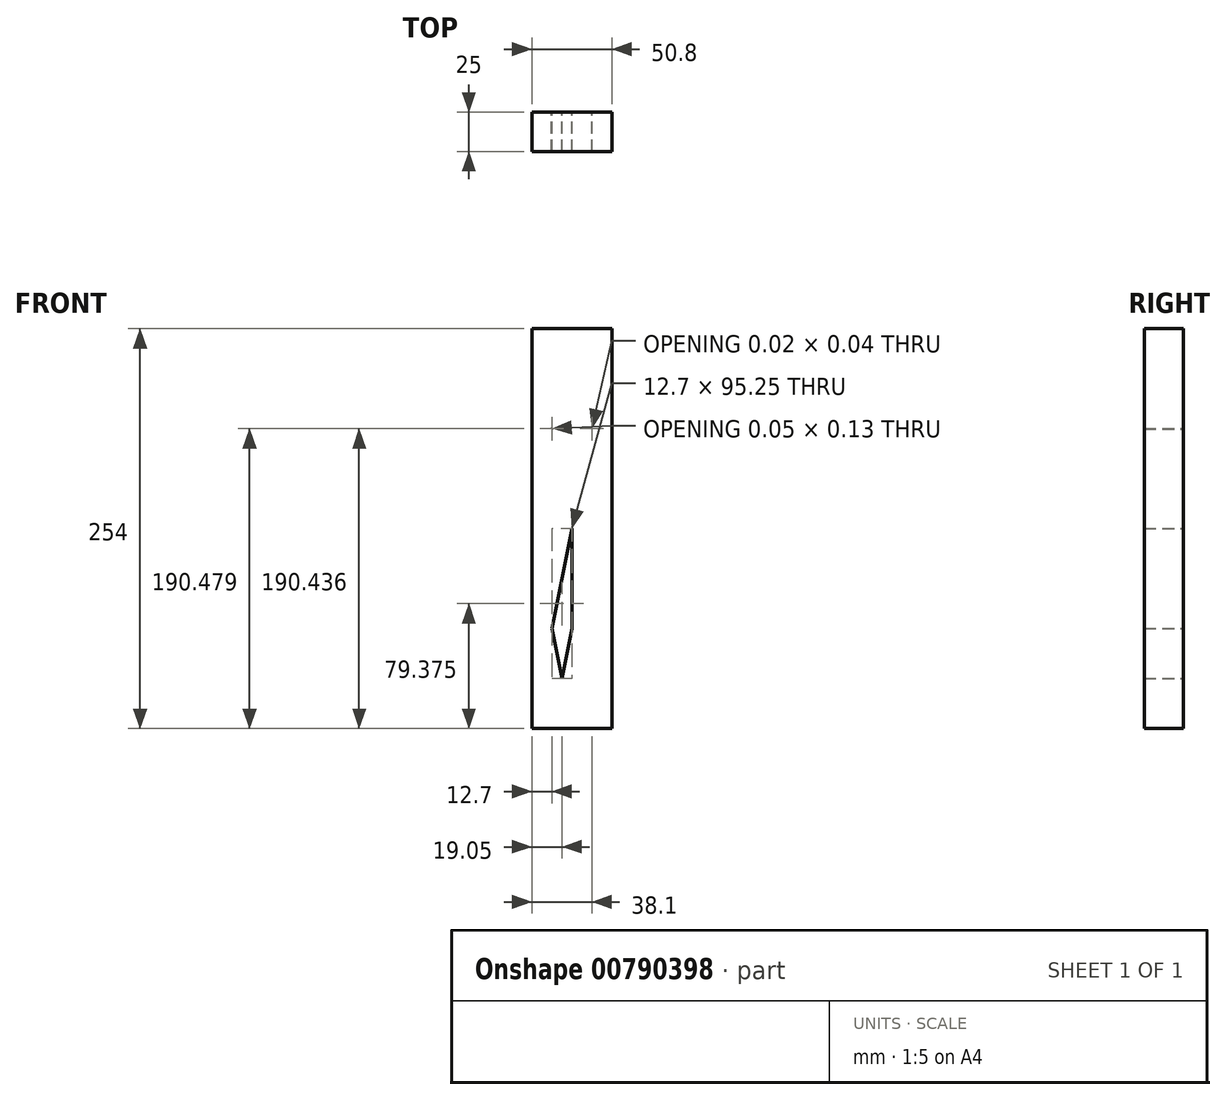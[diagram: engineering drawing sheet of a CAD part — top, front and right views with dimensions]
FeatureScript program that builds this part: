
annotation { "Feature Type Name" : "Feature", "Feature Type Description" : "" }
export const myFeature = defineFeature(function(context is Context, id is Id, definition is map)
    precondition{}
    {
        {
            var Q0;
            Q0=qCreatedBy(makeId("Front.planeOp"),FACE);
            var sketch = newSketch(context, id + "F0", { "sketchPlane" : qUnion([Q0])});
            skLineSegment(sketch, "E0.bottom", {"start": v(25.4, -127) * mm, "end": v(-25.4, -127) * mm});
            skLineSegment(sketch, "E0.top", {"start": v(25.4, 127) * mm, "end": v(-25.4, 127) * mm});
            skLineSegment(sketch, "E0.left", {"start": v(25.4, -127) * mm, "end": v(25.4, 127) * mm});
            skLineSegment(sketch, "E0.right", {"start": v(-25.4, -127) * mm, "end": v(-25.4, 127) * mm});
            skPoint(sketch, "E0.middle", {"position": v(0, 0) * mm});
            skLineSegment(sketch, "E1", {"start": v(-25.4, 127) * mm, "end": v(25.4, -127) * mm});
            skLineSegment(sketch, "E2", {"start": v(25.4, 127) * mm, "end": v(-25.4, -127) * mm});
            skLineSegment(sketch, "E3", {"start": v(0, 127) * mm, "end": v(0, -127) * mm});
            skLineSegment(sketch, "E4", {"start": v(0, -127) * mm, "end": v(-25.4, 0) * mm});
            skLineSegment(sketch, "E5", {"start": v(-25.4, 0) * mm, "end": v(25.4, 0) * mm});
            skLineSegment(sketch, "E6", {"start": v(25.4, 0) * mm, "end": v(0, -127) * mm});
            skLineSegment(sketch, "E7", {"start": v(-25.4, 0) * mm, "end": v(0, 127) * mm});
            skLineSegment(sketch, "E8", {"start": v(0, 127) * mm, "end": v(25.4, 0) * mm});
            skLineSegment(sketch, "E9", {"start": v(-12.7, 63.5) * mm, "end": v(-12.7, 0) * mm});
            skLineSegment(sketch, "E10", {"start": v(-12.7, 0) * mm, "end": v(-12.7, 127) * mm});
            skLineSegment(sketch, "E11", {"start": v(12.7, 0) * mm, "end": v(12.7, 127) * mm});
            skPoint(sketch, "E11.startSnap0", {"position": v(12.7, 63.5) * mm});
            skLineSegment(sketch, "E12", {"start": v(-12.7, 0) * mm, "end": v(-12.7, -127) * mm});
            skLineSegment(sketch, "E13", {"start": v(-12.7, -127) * mm, "end": v(12.7, 0) * mm});
            skLineSegment(sketch, "E14", {"start": v(12.7, 0) * mm, "end": v(12.7, -127) * mm});
            skLineSegment(sketch, "E15", {"start": v(-25.4, -63.5) * mm, "end": v(25.4, -63.5) * mm});
            skPoint(sketch, "E15.startSnap0", {"position": v(-12.7, -63.5) * mm});
            skPoint(sketch, "E15.endSnap0", {"position": v(12.7, -63.5) * mm});
            skLineSegment(sketch, "E16", {"start": v(-25.4, 63.33) * mm, "end": v(25.4, 63.5) * mm});
            skSolve(sketch);
        }
        {
            var Q0;
            {var subQ1=sQuery(id+"F0.wireOp",EDGE,"E0.left");var subQ3=sQuery(id+"F0.wireOp",EDGE,"E16");var subQ4=makeQuery(id+"F0.imprint","INTERSECT",VERTEX,{"derivedFrom":[subQ1,subQ3]});Q0=makeQuery(id+"F0.imprint","IMPRINT",FACE,{"disambiguationData":[TD([[makeQuery(id+"F0.imprint","IMPRINT",EDGE,{"disambiguationData":[TD([[subQ4,1.0]])],"derivedFrom":subQ3}),1.0]])]});}
            var Q1;
            {var subQ0=sQuery(id+"F0.wireOp",EDGE,"E13");var subQ1=sQuery(id+"F0.wireOp",EDGE,"E1");var subQ2=makeQuery(id+"F0.imprint","INTERSECT",VERTEX,{"derivedFrom":[subQ1,subQ0]});Q1=makeQuery(id+"F0.imprint","IMPRINT",FACE,{"disambiguationData":[TD([[makeQuery(id+"F0.imprint","IMPRINT",EDGE,{"disambiguationData":[TD([[subQ2,1.0]])],"derivedFrom":subQ1}),1.0]])]});}
            var Q2;
            {var subQ1=sQuery(id+"F0.wireOp",EDGE,"E0.bottom");var subQ3=sQuery(id+"F0.wireOp",EDGE,"E14");var subQ4=makeQuery(id+"F0.imprint","INTERSECT",VERTEX,{"derivedFrom":[subQ1,subQ3]});Q2=makeQuery(id+"F0.imprint","IMPRINT",FACE,{"disambiguationData":[TD([[makeQuery(id+"F0.imprint","IMPRINT",EDGE,{"disambiguationData":[TD([[subQ4,1.0]])],"derivedFrom":subQ1}),-1.0]])]});}
            var Q3;
            {var subQ1=sQuery(id+"F0.wireOp",EDGE,"E0.top");var subQ3=sQuery(id+"F0.wireOp",EDGE,"E11");var subQ4=makeQuery(id+"F0.imprint","INTERSECT",VERTEX,{"derivedFrom":[subQ1,subQ3]});Q3=makeQuery(id+"F0.imprint","IMPRINT",FACE,{"disambiguationData":[TD([[makeQuery(id+"F0.imprint","IMPRINT",EDGE,{"disambiguationData":[TD([[subQ4,1.0]])],"derivedFrom":subQ1}),1.0]])]});}
            var Q4;
            {var subQ1=sQuery(id+"F0.wireOp",EDGE,"E0.bottom");var subQ3=sQuery(id+"F0.wireOp",EDGE,"E14");var subQ4=makeQuery(id+"F0.imprint","INTERSECT",VERTEX,{"derivedFrom":[subQ1,subQ3]});Q4=makeQuery(id+"F0.imprint","IMPRINT",FACE,{"disambiguationData":[TD([[makeQuery(id+"F0.imprint","IMPRINT",EDGE,{"disambiguationData":[TD([[subQ4,-1.0]])],"derivedFrom":subQ1}),-1.0]])]});}
            var Q5;
            {var subQ0=sQuery(id+"F0.wireOp",EDGE,"E13");var subQ1=sQuery(id+"F0.wireOp",EDGE,"E1");var subQ2=makeQuery(id+"F0.imprint","INTERSECT",VERTEX,{"derivedFrom":[subQ1,subQ0]});Q5=makeQuery(id+"F0.imprint","IMPRINT",FACE,{"disambiguationData":[TD([[makeQuery(id+"F0.imprint","IMPRINT",EDGE,{"disambiguationData":[TD([[subQ2,1.0]])],"derivedFrom":subQ0}),1.0]])]});}
            var Q6;
            {var subQ0=sQuery(id+"F0.wireOp",EDGE,"E13");var subQ1=sQuery(id+"F0.wireOp",EDGE,"E4");var subQ2=makeQuery(id+"F0.imprint","INTERSECT",VERTEX,{"derivedFrom":[subQ1,subQ0]});Q6=makeQuery(id+"F0.imprint","IMPRINT",FACE,{"disambiguationData":[TD([[makeQuery(id+"F0.imprint","IMPRINT",EDGE,{"disambiguationData":[TD([[subQ2,1.0]])],"derivedFrom":subQ0}),1.0]])]});}
            var Q7;
            {var subQ1=sQuery(id+"F0.wireOp",EDGE,"E0.left");var subQ3=sQuery(id+"F0.wireOp",EDGE,"E15");var subQ4=makeQuery(id+"F0.imprint","INTERSECT",VERTEX,{"derivedFrom":[subQ1,subQ3]});Q7=makeQuery(id+"F0.imprint","IMPRINT",FACE,{"disambiguationData":[TD([[makeQuery(id+"F0.imprint","IMPRINT",EDGE,{"disambiguationData":[TD([[subQ4,1.0]])],"derivedFrom":subQ1}),1.0]])]});}
            var Q8;
            {var subQ1=sQuery(id+"F0.wireOp",EDGE,"E0.left");var subQ3=sQuery(id+"F0.wireOp",EDGE,"E15");var subQ4=makeQuery(id+"F0.imprint","INTERSECT",VERTEX,{"derivedFrom":[subQ1,subQ3]});Q8=makeQuery(id+"F0.imprint","IMPRINT",FACE,{"disambiguationData":[TD([[makeQuery(id+"F0.imprint","IMPRINT",EDGE,{"disambiguationData":[TD([[subQ4,-1.0]])],"derivedFrom":subQ1}),1.0]])]});}
            var Q9;
            {var subQ0=sQuery(id+"F0.wireOp",EDGE,"E16");var subQ1=sQuery(id+"F0.wireOp",EDGE,"E2");var subQ2=makeQuery(id+"F0.imprint","INTERSECT",VERTEX,{"derivedFrom":[subQ1,subQ0]});Q9=makeQuery(id+"F0.imprint","IMPRINT",FACE,{"disambiguationData":[TD([[makeQuery(id+"F0.imprint","IMPRINT",EDGE,{"disambiguationData":[TD([[subQ2,-1.0]])],"derivedFrom":subQ0}),-1.0]])]});}
            var Q10;
            {var subQ1=sQuery(id+"F0.wireOp",EDGE,"E0.right");var subQ3=sQuery(id+"F0.wireOp",EDGE,"E15");var subQ4=makeQuery(id+"F0.imprint","INTERSECT",VERTEX,{"derivedFrom":[subQ1,subQ3]});Q10=makeQuery(id+"F0.imprint","IMPRINT",FACE,{"disambiguationData":[TD([[makeQuery(id+"F0.imprint","IMPRINT",EDGE,{"disambiguationData":[TD([[subQ4,1.0]])],"derivedFrom":subQ1}),-1.0]])]});}
            var Q11;
            {var subQ0=sQuery(id+"F0.wireOp",EDGE,"E2");var subQ1=sQuery(id+"F0.wireOp",EDGE,"E0.bottom");var subQ2=makeQuery(id+"F0.imprint","INTERSECT",VERTEX,{"derivedFrom":[subQ1,sQuery(id+"F0.wireOp",EDGE,"E0.right"),subQ0]});Q11=makeQuery(id+"F0.imprint","IMPRINT",FACE,{"disambiguationData":[TD([[makeQuery(id+"F0.imprint","IMPRINT",EDGE,{"disambiguationData":[TD([[subQ2,1.0]])],"derivedFrom":subQ1}),-1.0]])]});}
            var Q12;
            {var subQ0=sQuery(id+"F0.wireOp",EDGE,"E5");var subQ3=sQuery(id+"F0.wireOp",EDGE,"E12");var subQ5=makeQuery(id+"F0.imprint","INTERSECT",VERTEX,{"derivedFrom":[subQ0,sQuery(id+"F0.wireOp",EDGE,"E10"),subQ3]});Q12=makeQuery(id+"F0.imprint","IMPRINT",FACE,{"disambiguationData":[TD([[makeQuery(id+"F0.imprint","IMPRINT",EDGE,{"disambiguationData":[TD([[subQ5,-1.0]])],"derivedFrom":subQ0}),-1.0]])]});}
            var Q13;
            {var subQ1=sQuery(id+"F0.wireOp",EDGE,"E0.top");var subQ3=sQuery(id+"F0.wireOp",EDGE,"E10");var subQ4=makeQuery(id+"F0.imprint","INTERSECT",VERTEX,{"derivedFrom":[subQ1,subQ3]});Q13=makeQuery(id+"F0.imprint","IMPRINT",FACE,{"disambiguationData":[TD([[makeQuery(id+"F0.imprint","IMPRINT",EDGE,{"disambiguationData":[TD([[subQ4,-1.0]])],"derivedFrom":subQ1}),1.0]])]});}
            var Q14;
            {var subQ0=sQuery(id+"F0.wireOp",EDGE,"E16");var subQ1=sQuery(id+"F0.wireOp",EDGE,"E1");var subQ2=makeQuery(id+"F0.imprint","INTERSECT",VERTEX,{"derivedFrom":[subQ1,subQ0]});Q14=makeQuery(id+"F0.imprint","IMPRINT",FACE,{"disambiguationData":[TD([[makeQuery(id+"F0.imprint","IMPRINT",EDGE,{"disambiguationData":[TD([[subQ2,1.0]])],"derivedFrom":subQ0}),-1.0]])]});}
            var Q15;
            {var subQ0=sQuery(id+"F0.wireOp",EDGE,"E13");var subQ1=sQuery(id+"F0.wireOp",EDGE,"E1");var subQ2=makeQuery(id+"F0.imprint","INTERSECT",VERTEX,{"derivedFrom":[subQ1,subQ0]});Q15=makeQuery(id+"F0.imprint","IMPRINT",FACE,{"disambiguationData":[TD([[makeQuery(id+"F0.imprint","IMPRINT",EDGE,{"disambiguationData":[TD([[subQ2,1.0]])],"derivedFrom":subQ0}),-1.0]])]});}
            var Q16;
            {var subQ1=sQuery(id+"F0.wireOp",EDGE,"E0.top");var subQ3=sQuery(id+"F0.wireOp",EDGE,"E11");var subQ4=makeQuery(id+"F0.imprint","INTERSECT",VERTEX,{"derivedFrom":[subQ1,subQ3]});Q16=makeQuery(id+"F0.imprint","IMPRINT",FACE,{"disambiguationData":[TD([[makeQuery(id+"F0.imprint","IMPRINT",EDGE,{"disambiguationData":[TD([[subQ4,1.0]])],"derivedFrom":subQ3}),1.0]])]});}
            var Q17;
            {var subQ1=sQuery(id+"F0.wireOp",EDGE,"E0.left");var subQ3=sQuery(id+"F0.wireOp",EDGE,"E16");var subQ4=makeQuery(id+"F0.imprint","INTERSECT",VERTEX,{"derivedFrom":[subQ1,subQ3]});Q17=makeQuery(id+"F0.imprint","IMPRINT",FACE,{"disambiguationData":[TD([[makeQuery(id+"F0.imprint","IMPRINT",EDGE,{"disambiguationData":[TD([[subQ4,1.0]])],"derivedFrom":subQ3}),-1.0]])]});}
            var Q18;
            {var subQ1=sQuery(id+"F0.wireOp",EDGE,"E0.right");var subQ3=sQuery(id+"F0.wireOp",EDGE,"E16");var subQ4=makeQuery(id+"F0.imprint","INTERSECT",VERTEX,{"derivedFrom":[subQ1,subQ3]});Q18=makeQuery(id+"F0.imprint","IMPRINT",FACE,{"disambiguationData":[TD([[makeQuery(id+"F0.imprint","IMPRINT",EDGE,{"disambiguationData":[TD([[subQ4,-1.0]])],"derivedFrom":subQ3}),-1.0]])]});}
            var Q19;
            {var subQ0=sQuery(id+"F0.wireOp",EDGE,"E13");var subQ1=sQuery(id+"F0.wireOp",EDGE,"E1");var subQ2=makeQuery(id+"F0.imprint","INTERSECT",VERTEX,{"derivedFrom":[subQ1,subQ0]});Q19=makeQuery(id+"F0.imprint","IMPRINT",FACE,{"disambiguationData":[TD([[makeQuery(id+"F0.imprint","IMPRINT",EDGE,{"disambiguationData":[TD([[subQ2,-1.0]])],"derivedFrom":subQ1}),1.0]])]});}
            var Q20;
            {var subQ0=sQuery(id+"F0.wireOp",EDGE,"E4");var subQ3=sQuery(id+"F0.wireOp",EDGE,"E13");var subQ5=makeQuery(id+"F0.imprint","INTERSECT",VERTEX,{"derivedFrom":[subQ0,subQ3]});Q20=makeQuery(id+"F0.imprint","IMPRINT",FACE,{"disambiguationData":[TD([[makeQuery(id+"F0.imprint","IMPRINT",EDGE,{"disambiguationData":[TD([[subQ5,-1.0]])],"derivedFrom":subQ3}),-1.0]])]});}
            var Q21;
            {var subQ1=sQuery(id+"F0.wireOp",EDGE,"E0.right");var subQ3=sQuery(id+"F0.wireOp",EDGE,"E16");var subQ4=makeQuery(id+"F0.imprint","INTERSECT",VERTEX,{"derivedFrom":[subQ1,subQ3]});Q21=makeQuery(id+"F0.imprint","IMPRINT",FACE,{"disambiguationData":[TD([[makeQuery(id+"F0.imprint","IMPRINT",EDGE,{"disambiguationData":[TD([[subQ4,-1.0]])],"derivedFrom":subQ3}),1.0]])]});}
            var Q22;
            {var subQ0=sQuery(id+"F0.wireOp",EDGE,"E4");var subQ3=sQuery(id+"F0.wireOp",EDGE,"E13");var subQ5=makeQuery(id+"F0.imprint","INTERSECT",VERTEX,{"derivedFrom":[subQ0,subQ3]});Q22=makeQuery(id+"F0.imprint","IMPRINT",FACE,{"disambiguationData":[TD([[makeQuery(id+"F0.imprint","IMPRINT",EDGE,{"disambiguationData":[TD([[subQ5,1.0]])],"derivedFrom":subQ3}),-1.0]])]});}
            var Q23;
            Q23 = qSketchRegion(id + "F0", true);
            var Q24;
            {var subQ0=sQuery(id+"F0.wireOp",EDGE,"E16");var subQ1=sQuery(id+"F0.wireOp",EDGE,"E1");var subQ2=makeQuery(id+"F0.imprint","INTERSECT",VERTEX,{"derivedFrom":[subQ1,subQ0]});Q24=makeQuery(id+"F0.imprint","IMPRINT",FACE,{"disambiguationData":[TD([[makeQuery(id+"F0.imprint","IMPRINT",EDGE,{"disambiguationData":[TD([[subQ2,-1.0]])],"derivedFrom":subQ0}),-1.0]])]});}
            var Q25;
            {var subQ1=sQuery(id+"F0.wireOp",EDGE,"E0.right");var subQ3=sQuery(id+"F0.wireOp",EDGE,"E15");var subQ4=makeQuery(id+"F0.imprint","INTERSECT",VERTEX,{"derivedFrom":[subQ1,subQ3]});Q25=makeQuery(id+"F0.imprint","IMPRINT",FACE,{"disambiguationData":[TD([[makeQuery(id+"F0.imprint","IMPRINT",EDGE,{"disambiguationData":[TD([[subQ4,-1.0]])],"derivedFrom":subQ1}),-1.0]])]});}
            var Q26;
            {var subQ0=sQuery(id+"F0.wireOp",EDGE,"E16");var subQ1=sQuery(id+"F0.wireOp",EDGE,"E2");var subQ2=makeQuery(id+"F0.imprint","INTERSECT",VERTEX,{"derivedFrom":[subQ1,subQ0]});Q26=makeQuery(id+"F0.imprint","IMPRINT",FACE,{"disambiguationData":[TD([[makeQuery(id+"F0.imprint","IMPRINT",EDGE,{"disambiguationData":[TD([[subQ2,1.0]])],"derivedFrom":subQ0}),-1.0]])]});}
            var Q27;
            {var subQ1=sQuery(id+"F0.wireOp",EDGE,"E0.top");var subQ3=sQuery(id+"F0.wireOp",EDGE,"E10");var subQ4=makeQuery(id+"F0.imprint","INTERSECT",VERTEX,{"derivedFrom":[subQ1,subQ3]});Q27=makeQuery(id+"F0.imprint","IMPRINT",FACE,{"disambiguationData":[TD([[makeQuery(id+"F0.imprint","IMPRINT",EDGE,{"disambiguationData":[TD([[subQ4,1.0]])],"derivedFrom":subQ3}),-1.0]])]});}
            extrude(context, id + "F1", {"entities" : qUnion([Q0, Q1, Q2, Q3, Q4, Q5, Q6, Q7, Q8, Q9, Q10, Q11, Q12, Q13, Q14, Q15, Q16, Q17, Q18, Q19, Q20, Q21, Q22, Q23, Q24, Q25, Q26, Q27]), "depth" : 25 * mm, "offsetDistance" : 25 * mm});
        }
        {
            var Q0;
            {var subQ0=sQuery(id+"F0.wireOp",EDGE,"E16");var subQ1=sQuery(id+"F0.wireOp",EDGE,"E2");var subQ2=makeQuery(id+"F0.imprint","INTERSECT",VERTEX,{"derivedFrom":[subQ1,subQ0]});Q0=makeQuery(id+"F0.imprint","IMPRINT",FACE,{"disambiguationData":[TD([[makeQuery(id+"F0.imprint","IMPRINT",EDGE,{"disambiguationData":[TD([[subQ2,-1.0]])],"derivedFrom":subQ0}),-1.0]])]});}
            var Q1;
            {var subQ0=sQuery(id+"F0.wireOp",EDGE,"E13");var subQ1=sQuery(id+"F0.wireOp",EDGE,"E1");var subQ2=makeQuery(id+"F0.imprint","INTERSECT",VERTEX,{"derivedFrom":[subQ1,subQ0]});Q1=makeQuery(id+"F0.imprint","IMPRINT",FACE,{"disambiguationData":[TD([[makeQuery(id+"F0.imprint","IMPRINT",EDGE,{"disambiguationData":[TD([[subQ2,-1.0]])],"derivedFrom":subQ1}),1.0]])]});}
            var Q2;
            {var subQ0=sQuery(id+"F0.wireOp",EDGE,"E8");var subQ5=sQuery(id+"F0.wireOp",EDGE,"E16");var subQ6=makeQuery(id+"F0.imprint","INTERSECT",VERTEX,{"derivedFrom":[subQ0,subQ5]});Q2=makeQuery(id+"F0.imprint","IMPRINT",FACE,{"disambiguationData":[TD([[makeQuery(id+"F0.imprint","IMPRINT",EDGE,{"disambiguationData":[TD([[subQ6,1.0]])],"derivedFrom":subQ5}),-1.0]])]});}
            var Q3;
            {var subQ0=sQuery(id+"F0.wireOp",EDGE,"E7");var subQ5=sQuery(id+"F0.wireOp",EDGE,"E16");var subQ6=makeQuery(id+"F0.imprint","INTERSECT",VERTEX,{"derivedFrom":[subQ0,subQ5]});Q3=makeQuery(id+"F0.imprint","IMPRINT",FACE,{"disambiguationData":[TD([[makeQuery(id+"F0.imprint","IMPRINT",EDGE,{"disambiguationData":[TD([[subQ6,-1.0]])],"derivedFrom":subQ5}),-1.0]])]});}
            var Q4;
            {var subQ0=sQuery(id+"F0.wireOp",EDGE,"E13");var subQ1=sQuery(id+"F0.wireOp",EDGE,"E1");var subQ2=makeQuery(id+"F0.imprint","INTERSECT",VERTEX,{"derivedFrom":[subQ1,subQ0]});Q4=makeQuery(id+"F0.imprint","IMPRINT",FACE,{"disambiguationData":[TD([[makeQuery(id+"F0.imprint","IMPRINT",EDGE,{"disambiguationData":[TD([[subQ2,1.0]])],"derivedFrom":subQ1}),1.0]])]});}
            var Q5;
            {var subQ0=sQuery(id+"F0.wireOp",EDGE,"E16");var subQ1=sQuery(id+"F0.wireOp",EDGE,"E1");var subQ2=makeQuery(id+"F0.imprint","INTERSECT",VERTEX,{"derivedFrom":[subQ1,subQ0]});Q5=makeQuery(id+"F0.imprint","IMPRINT",FACE,{"disambiguationData":[TD([[makeQuery(id+"F0.imprint","IMPRINT",EDGE,{"disambiguationData":[TD([[subQ2,1.0]])],"derivedFrom":subQ0}),-1.0]])]});}
            var Q6;
            {var subQ0=sQuery(id+"F0.wireOp",EDGE,"E6");var subQ1=sQuery(id+"F0.wireOp",EDGE,"E5");var subQ2=makeQuery(id+"F0.imprint","INTERSECT",VERTEX,{"derivedFrom":[sQuery(id+"F0.wireOp",EDGE,"E0.left"),subQ1,subQ0,sQuery(id+"F0.wireOp",EDGE,"E8")]});Q6=makeQuery(id+"F0.imprint","IMPRINT",FACE,{"disambiguationData":[TD([[makeQuery(id+"F0.imprint","IMPRINT",EDGE,{"disambiguationData":[TD([[subQ2,1.0]])],"derivedFrom":subQ1}),-1.0]])]});}
            var Q7;
            {var subQ0=sQuery(id+"F0.wireOp",EDGE,"E5");var subQ3=sQuery(id+"F0.wireOp",EDGE,"E12");var subQ5=makeQuery(id+"F0.imprint","INTERSECT",VERTEX,{"derivedFrom":[subQ0,sQuery(id+"F0.wireOp",EDGE,"E10"),subQ3]});Q7=makeQuery(id+"F0.imprint","IMPRINT",FACE,{"disambiguationData":[TD([[makeQuery(id+"F0.imprint","IMPRINT",EDGE,{"disambiguationData":[TD([[subQ5,-1.0]])],"derivedFrom":subQ0}),-1.0]])]});}
            var Q8;
            {var subQ0=sQuery(id+"F0.wireOp",EDGE,"E5");var subQ3=sQuery(id+"F0.wireOp",EDGE,"E12");var subQ5=makeQuery(id+"F0.imprint","INTERSECT",VERTEX,{"derivedFrom":[subQ0,sQuery(id+"F0.wireOp",EDGE,"E10"),subQ3]});Q8=makeQuery(id+"F0.imprint","IMPRINT",FACE,{"disambiguationData":[TD([[makeQuery(id+"F0.imprint","IMPRINT",EDGE,{"disambiguationData":[TD([[subQ5,1.0]])],"derivedFrom":subQ0}),-1.0]])]});}
            extrude(context, id + "F2", {"entities" : qUnion([Q0, Q1, Q2, Q3, Q4, Q5, Q6, Q7, Q8]), "operationType" : NewBodyOperationType.REMOVE, "oppositeDirection" : true, "depth" : 151.73 * mm, "offsetDistance" : 25 * mm});
        }
    });
